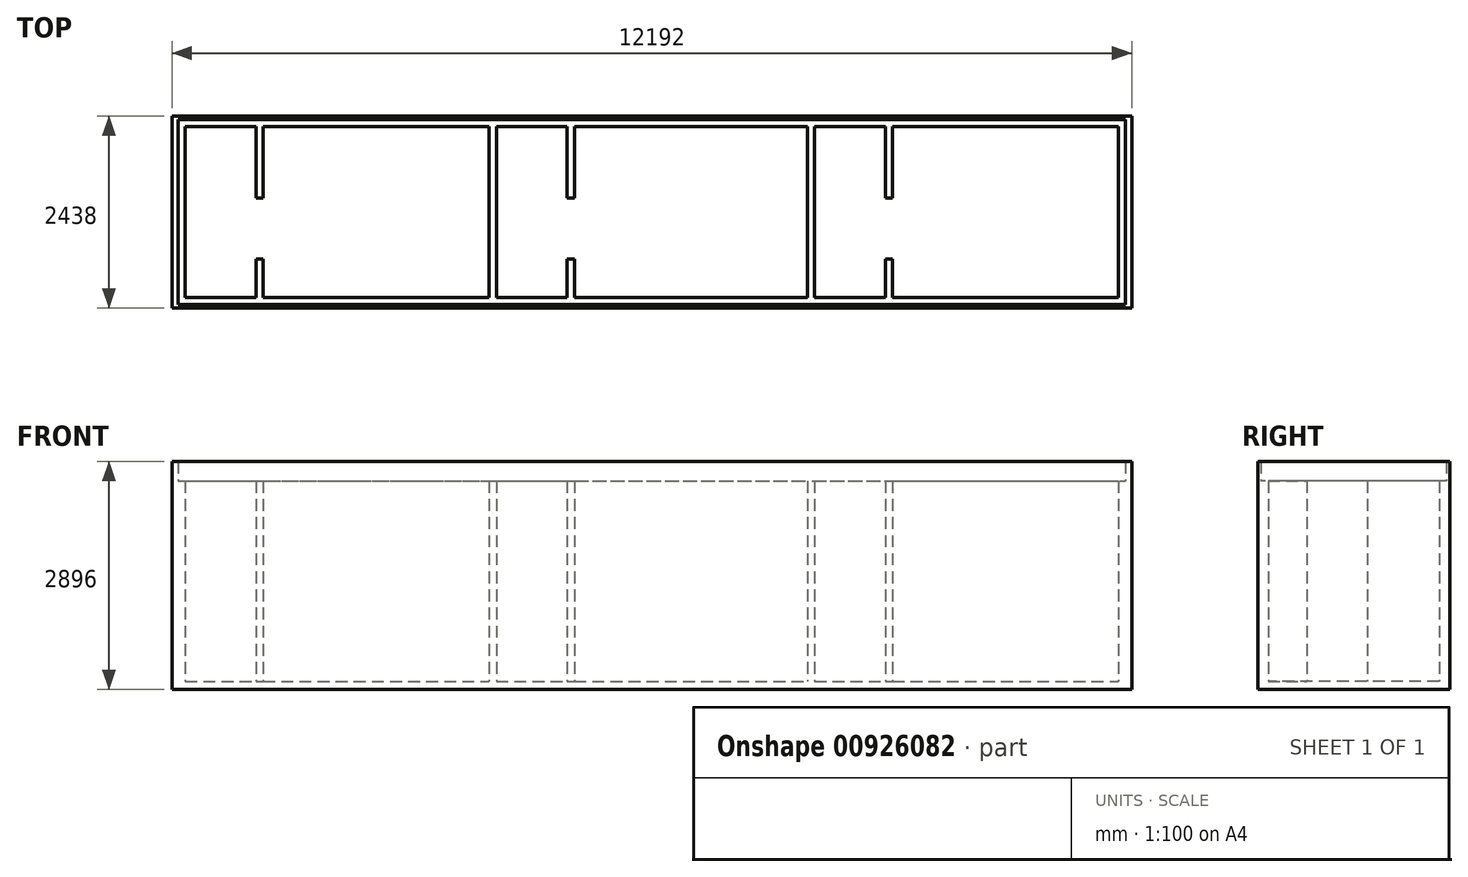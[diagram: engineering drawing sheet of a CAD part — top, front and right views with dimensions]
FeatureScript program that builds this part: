
annotation { "Feature Type Name" : "Feature", "Feature Type Description" : "" }
export const myFeature = defineFeature(function(context is Context, id is Id, definition is map)
    precondition{}
    {
        {
            var Q0;
            Q0=qCreatedBy(makeId("Top.planeOp"),FACE);
            var sketch = newSketch(context, id + "F0", { "sketchPlane" : qUnion([Q0])});
            skLineSegment(sketch, "E0.bottom", {"start": v(-6016, 1176) * mm, "end": v(6016, 1176) * mm});
            skLineSegment(sketch, "E0.top", {"start": v(-6016, -1176) * mm, "end": v(6016, -1176) * mm});
            skLineSegment(sketch, "E0.left", {"start": v(-6016, 1176) * mm, "end": v(-6016, -1176) * mm});
            skLineSegment(sketch, "E0.right", {"start": v(6016, 1176) * mm, "end": v(6016, -1176) * mm});
            skPoint(sketch, "E0.middle", {"position": v(0, 0) * mm});
            skLineSegment(sketch, "E1.bottom", {"start": v(-6096, 1219) * mm, "end": v(6096, 1219) * mm});
            skLineSegment(sketch, "E1.top", {"start": v(-6096, -1219) * mm, "end": v(6096, -1219) * mm});
            skLineSegment(sketch, "E1.left", {"start": v(-6096, 1219) * mm, "end": v(-6096, -1219) * mm});
            skLineSegment(sketch, "E1.right", {"start": v(6096, 1219) * mm, "end": v(6096, -1219) * mm});
            skSolve(sketch);
        }
        {
            var Q0;
            Q0=makeQuery(id+"F0.imprint","IMPRINT",FACE,{"disambiguationData":[TD([[makeQuery(id+"F0.imprint","IMPRINT",EDGE,{"derivedFrom":sQuery(id+"F0.wireOp",EDGE,"E0.bottom")}),1.0]])]});
            extrude(context, id + "F1", {"entities" : qUnion([Q0]), "depth" : 2896 * mm, "offsetDistance" : 25 * mm});
        }
        {
            var Q0;
            Q0=makeQuery(id+"F0.imprint","IMPRINT",FACE,{"disambiguationData":[TD([[makeQuery(id+"F0.imprint","IMPRINT",EDGE,{"derivedFrom":sQuery(id+"F0.wireOp",EDGE,"E0.bottom")}),-1.0]])]});
            extrude(context, id + "F2", {"entities" : qUnion([Q0]), "operationType" : NewBodyOperationType.ADD, "depth" : 99 * mm, "offsetDistance" : 25 * mm});
        }
        {
            var Q0;
            Q0=makeQuery(id+"F2.opExtrude","CAP_FACE",FACE,{"disambiguationData":[OSD([sQuery(id+"F0.wireOp",EDGE,"E0.bottom"),sQuery(id+"F0.wireOp",EDGE,"E0.top"),sQuery(id+"F0.wireOp",EDGE,"E0.left"),sQuery(id+"F0.wireOp",EDGE,"E0.right")])],"isStart":false});
            var sketch = newSketch(context, id + "F3", { "sketchPlane" : qUnion([Q0])});
            skLineSegment(sketch, "E2.bottom", {"start": v(-2065, 1176) * mm, "end": v(-1975, 1176) * mm});
            skLineSegment(sketch, "E2.top", {"start": v(-2065, -1176) * mm, "end": v(-1975, -1176) * mm});
            skLineSegment(sketch, "E2.left", {"start": v(-2065, 1176) * mm, "end": v(-2065, -1176) * mm});
            skLineSegment(sketch, "E2.right", {"start": v(-1975, 1176) * mm, "end": v(-1975, -1176) * mm});
            skLineSegment(sketch, "E3.bottom", {"start": v(1976, 1176) * mm, "end": v(2066, 1176) * mm});
            skLineSegment(sketch, "E3.top", {"start": v(1976, -1176) * mm, "end": v(2066, -1176) * mm});
            skLineSegment(sketch, "E3.left", {"start": v(1976, 1176) * mm, "end": v(1976, -1176) * mm});
            skLineSegment(sketch, "E3.right", {"start": v(2066, 1176) * mm, "end": v(2066, -1176) * mm});
            skLineSegment(sketch, "E4.bottom", {"start": v(-5026, 1176) * mm, "end": v(-4936, 1176) * mm});
            skLineSegment(sketch, "E4.top", {"start": v(-5026, 176) * mm, "end": v(-4936, 176) * mm});
            skLineSegment(sketch, "E4.left", {"start": v(-5026, 1176) * mm, "end": v(-5026, 176) * mm});
            skLineSegment(sketch, "E4.right", {"start": v(-4936, 1176) * mm, "end": v(-4936, 176) * mm});
            skLineSegment(sketch, "E5.bottom", {"start": v(-5026, -1176) * mm, "end": v(-4936, -1176) * mm});
            skLineSegment(sketch, "E5.top", {"start": v(-5026, -594) * mm, "end": v(-4936, -594) * mm});
            skLineSegment(sketch, "E5.left", {"start": v(-5026, -1176) * mm, "end": v(-5026, -594) * mm});
            skLineSegment(sketch, "E5.right", {"start": v(-4936, -1176) * mm, "end": v(-4936, -594) * mm});
            skLineSegment(sketch, "E6.bottom", {"start": v(-1075, 1176) * mm, "end": v(-985, 1176) * mm});
            skLineSegment(sketch, "E6.top", {"start": v(-1075, 176) * mm, "end": v(-985, 176) * mm});
            skLineSegment(sketch, "E6.left", {"start": v(-1075, 1176) * mm, "end": v(-1075, 176) * mm});
            skLineSegment(sketch, "E6.right", {"start": v(-985, 1176) * mm, "end": v(-985, 176) * mm});
            skLineSegment(sketch, "E7.bottom", {"start": v(-1075, -594) * mm, "end": v(-985, -594) * mm});
            skLineSegment(sketch, "E7.top", {"start": v(-1075, -1176) * mm, "end": v(-985, -1176) * mm});
            skLineSegment(sketch, "E7.left", {"start": v(-1075, -594) * mm, "end": v(-1075, -1176) * mm});
            skLineSegment(sketch, "E7.right", {"start": v(-985, -594) * mm, "end": v(-985, -1176) * mm});
            skLineSegment(sketch, "E8.bottom", {"start": v(2966, 1176) * mm, "end": v(3056, 1176) * mm});
            skLineSegment(sketch, "E8.top", {"start": v(2966, 176) * mm, "end": v(3056, 176) * mm});
            skLineSegment(sketch, "E8.left", {"start": v(2966, 1176) * mm, "end": v(2966, 176) * mm});
            skLineSegment(sketch, "E8.right", {"start": v(3056, 1176) * mm, "end": v(3056, 176) * mm});
            skLineSegment(sketch, "E9.bottom", {"start": v(2966, -1176) * mm, "end": v(3056, -1176) * mm});
            skLineSegment(sketch, "E9.top", {"start": v(2966, -594) * mm, "end": v(3056, -594) * mm});
            skLineSegment(sketch, "E9.left", {"start": v(2966, -1176) * mm, "end": v(2966, -594) * mm});
            skLineSegment(sketch, "E9.right", {"start": v(3056, -1176) * mm, "end": v(3056, -594) * mm});
            skLineSegment(sketch, "E10.bottom", {"start": v(-6016, 1176) * mm, "end": v(6016, 1176) * mm});
            skLineSegment(sketch, "E10.top", {"start": v(-6016, 1086) * mm, "end": v(6016, 1086) * mm});
            skLineSegment(sketch, "E10.left", {"start": v(-6016, 1176) * mm, "end": v(-6016, 1086) * mm});
            skLineSegment(sketch, "E10.right", {"start": v(6016, 1176) * mm, "end": v(6016, 1086) * mm});
            skLineSegment(sketch, "E11.bottom", {"start": v(6016, -1176) * mm, "end": v(-6016, -1176) * mm});
            skLineSegment(sketch, "E11.top", {"start": v(6016, -1086) * mm, "end": v(-6016, -1086) * mm});
            skLineSegment(sketch, "E11.left", {"start": v(6016, -1176) * mm, "end": v(6016, -1086) * mm});
            skLineSegment(sketch, "E11.right", {"start": v(-6016, -1176) * mm, "end": v(-6016, -1086) * mm});
            skLineSegment(sketch, "E12.bottom", {"start": v(-5926, -1086) * mm, "end": v(-6016, -1086) * mm});
            skLineSegment(sketch, "E12.top", {"start": v(-5926, 1086) * mm, "end": v(-6016, 1086) * mm});
            skLineSegment(sketch, "E12.left", {"start": v(-5926, -1086) * mm, "end": v(-5926, 1086) * mm});
            skLineSegment(sketch, "E12.right", {"start": v(-6016, -1086) * mm, "end": v(-6016, 1086) * mm});
            skLineSegment(sketch, "E13.bottom", {"start": v(6016, 1086) * mm, "end": v(5926, 1086) * mm});
            skLineSegment(sketch, "E13.top", {"start": v(6016, -1086) * mm, "end": v(5926, -1086) * mm});
            skLineSegment(sketch, "E13.left", {"start": v(6016, 1086) * mm, "end": v(6016, -1086) * mm});
            skLineSegment(sketch, "E13.right", {"start": v(5926, 1086) * mm, "end": v(5926, -1086) * mm});
            skSolve(sketch);
        }
        {
            var Q0;
            {var subQ2=sQuery(id+"F3.wireOp",EDGE,"E10.left");Q0=makeQuery(id+"F3.imprint","IMPRINT",FACE,{"disambiguationData":[TD([[makeQuery(id+"F3.imprint","IMPRINT",EDGE,{"derivedFrom":subQ2}),1.0]])]});}
            var Q1;
            {var subQ0=sQuery(id+"F3.wireOp",EDGE,"E4.bottom");Q1=makeQuery(id+"F3.imprint","IMPRINT",FACE,{"disambiguationData":[TD([[makeQuery(id+"F3.imprint","IMPRINT",EDGE,{"derivedFrom":subQ0}),-1.0]])]});}
            var Q2;
            {var subQ1=sQuery(id+"F3.wireOp",EDGE,"E2.left");var subQ3=sQuery(id+"F3.wireOp",EDGE,"E10.top");var subQ4=makeQuery(id+"F3.imprint","INTERSECT",VERTEX,{"derivedFrom":[subQ1,subQ3]});Q2=makeQuery(id+"F3.imprint","IMPRINT",FACE,{"disambiguationData":[TD([[makeQuery(id+"F3.imprint","IMPRINT",EDGE,{"disambiguationData":[TD([[subQ4,1.0]])],"derivedFrom":subQ3}),1.0]])]});}
            var Q3;
            {var subQ0=sQuery(id+"F3.wireOp",EDGE,"E4.top");Q3=makeQuery(id+"F3.imprint","IMPRINT",FACE,{"disambiguationData":[TD([[makeQuery(id+"F3.imprint","IMPRINT",EDGE,{"derivedFrom":subQ0}),1.0]])]});}
            var Q4;
            {var subQ0=sQuery(id+"F3.wireOp",EDGE,"E12.left");Q4=makeQuery(id+"F3.imprint","IMPRINT",FACE,{"disambiguationData":[TD([[makeQuery(id+"F3.imprint","IMPRINT",EDGE,{"derivedFrom":subQ0}),1.0]])]});}
            var Q5;
            {var subQ0=sQuery(id+"F3.wireOp",EDGE,"E11.right");Q5=makeQuery(id+"F3.imprint","IMPRINT",FACE,{"disambiguationData":[TD([[makeQuery(id+"F3.imprint","IMPRINT",EDGE,{"derivedFrom":subQ0}),1.0]])]});}
            var Q6;
            {var subQ0=sQuery(id+"F3.wireOp",EDGE,"E5.top");Q6=makeQuery(id+"F3.imprint","IMPRINT",FACE,{"disambiguationData":[TD([[makeQuery(id+"F3.imprint","IMPRINT",EDGE,{"derivedFrom":subQ0}),-1.0]])]});}
            var Q7;
            {var subQ0=sQuery(id+"F3.wireOp",EDGE,"E5.bottom");Q7=makeQuery(id+"F3.imprint","IMPRINT",FACE,{"disambiguationData":[TD([[makeQuery(id+"F3.imprint","IMPRINT",EDGE,{"derivedFrom":subQ0}),1.0]])]});}
            var Q8;
            {var subQ3=sQuery(id+"F3.wireOp",EDGE,"E11.top");var subQ5=sQuery(id+"F3.wireOp",EDGE,"E5.right");var subQ7=makeQuery(id+"F3.imprint","INTERSECT",VERTEX,{"derivedFrom":[subQ5,subQ3]});Q8=makeQuery(id+"F3.imprint","IMPRINT",FACE,{"disambiguationData":[TD([[makeQuery(id+"F3.imprint","IMPRINT",EDGE,{"disambiguationData":[TD([[subQ7,1.0]])],"derivedFrom":subQ3}),1.0]])]});}
            var Q9;
            {var subQ0=sQuery(id+"F3.wireOp",EDGE,"E10.top");var subQ1=sQuery(id+"F3.wireOp",EDGE,"E2.left");var subQ2=makeQuery(id+"F3.imprint","INTERSECT",VERTEX,{"derivedFrom":[subQ1,subQ0]});Q9=makeQuery(id+"F3.imprint","IMPRINT",FACE,{"disambiguationData":[TD([[makeQuery(id+"F3.imprint","IMPRINT",EDGE,{"disambiguationData":[TD([[subQ2,-1.0]])],"derivedFrom":subQ1}),1.0]])]});}
            var Q10;
            {var subQ0=sQuery(id+"F3.wireOp",EDGE,"E2.bottom");Q10=makeQuery(id+"F3.imprint","IMPRINT",FACE,{"disambiguationData":[TD([[makeQuery(id+"F3.imprint","IMPRINT",EDGE,{"derivedFrom":subQ0}),-1.0]])]});}
            var Q11;
            {var subQ1=sQuery(id+"F3.wireOp",EDGE,"E2.right");var subQ3=sQuery(id+"F3.wireOp",EDGE,"E10.top");var subQ4=makeQuery(id+"F3.imprint","INTERSECT",VERTEX,{"derivedFrom":[subQ1,subQ3]});Q11=makeQuery(id+"F3.imprint","IMPRINT",FACE,{"disambiguationData":[TD([[makeQuery(id+"F3.imprint","IMPRINT",EDGE,{"disambiguationData":[TD([[subQ4,-1.0]])],"derivedFrom":subQ3}),1.0]])]});}
            var Q12;
            {var subQ0=sQuery(id+"F3.wireOp",EDGE,"E6.bottom");Q12=makeQuery(id+"F3.imprint","IMPRINT",FACE,{"disambiguationData":[TD([[makeQuery(id+"F3.imprint","IMPRINT",EDGE,{"derivedFrom":subQ0}),-1.0]])]});}
            var Q13;
            {var subQ1=sQuery(id+"F3.wireOp",EDGE,"E3.left");var subQ3=sQuery(id+"F3.wireOp",EDGE,"E10.top");var subQ4=makeQuery(id+"F3.imprint","INTERSECT",VERTEX,{"derivedFrom":[subQ1,subQ3]});Q13=makeQuery(id+"F3.imprint","IMPRINT",FACE,{"disambiguationData":[TD([[makeQuery(id+"F3.imprint","IMPRINT",EDGE,{"disambiguationData":[TD([[subQ4,1.0]])],"derivedFrom":subQ3}),1.0]])]});}
            var Q14;
            {var subQ0=sQuery(id+"F3.wireOp",EDGE,"E6.top");Q14=makeQuery(id+"F3.imprint","IMPRINT",FACE,{"disambiguationData":[TD([[makeQuery(id+"F3.imprint","IMPRINT",EDGE,{"derivedFrom":subQ0}),1.0]])]});}
            var Q15;
            {var subQ1=sQuery(id+"F3.wireOp",EDGE,"E2.right");var subQ3=sQuery(id+"F3.wireOp",EDGE,"E11.top");var subQ4=makeQuery(id+"F3.imprint","INTERSECT",VERTEX,{"derivedFrom":[subQ1,subQ3]});Q15=makeQuery(id+"F3.imprint","IMPRINT",FACE,{"disambiguationData":[TD([[makeQuery(id+"F3.imprint","IMPRINT",EDGE,{"disambiguationData":[TD([[subQ4,1.0]])],"derivedFrom":subQ3}),1.0]])]});}
            var Q16;
            {var subQ0=sQuery(id+"F3.wireOp",EDGE,"E2.top");Q16=makeQuery(id+"F3.imprint","IMPRINT",FACE,{"disambiguationData":[TD([[makeQuery(id+"F3.imprint","IMPRINT",EDGE,{"derivedFrom":subQ0}),1.0]])]});}
            var Q17;
            {var subQ0=sQuery(id+"F3.wireOp",EDGE,"E7.bottom");Q17=makeQuery(id+"F3.imprint","IMPRINT",FACE,{"disambiguationData":[TD([[makeQuery(id+"F3.imprint","IMPRINT",EDGE,{"derivedFrom":subQ0}),-1.0]])]});}
            var Q18;
            {var subQ0=sQuery(id+"F3.wireOp",EDGE,"E7.top");Q18=makeQuery(id+"F3.imprint","IMPRINT",FACE,{"disambiguationData":[TD([[makeQuery(id+"F3.imprint","IMPRINT",EDGE,{"derivedFrom":subQ0}),1.0]])]});}
            var Q19;
            {var subQ1=sQuery(id+"F3.wireOp",EDGE,"E3.left");var subQ3=sQuery(id+"F3.wireOp",EDGE,"E11.top");var subQ4=makeQuery(id+"F3.imprint","INTERSECT",VERTEX,{"derivedFrom":[subQ1,subQ3]});Q19=makeQuery(id+"F3.imprint","IMPRINT",FACE,{"disambiguationData":[TD([[makeQuery(id+"F3.imprint","IMPRINT",EDGE,{"disambiguationData":[TD([[subQ4,-1.0]])],"derivedFrom":subQ3}),1.0]])]});}
            var Q20;
            {var subQ0=sQuery(id+"F3.wireOp",EDGE,"E10.top");var subQ1=sQuery(id+"F3.wireOp",EDGE,"E3.left");var subQ2=makeQuery(id+"F3.imprint","INTERSECT",VERTEX,{"derivedFrom":[subQ1,subQ0]});Q20=makeQuery(id+"F3.imprint","IMPRINT",FACE,{"disambiguationData":[TD([[makeQuery(id+"F3.imprint","IMPRINT",EDGE,{"disambiguationData":[TD([[subQ2,-1.0]])],"derivedFrom":subQ1}),1.0]])]});}
            var Q21;
            {var subQ0=sQuery(id+"F3.wireOp",EDGE,"E3.bottom");Q21=makeQuery(id+"F3.imprint","IMPRINT",FACE,{"disambiguationData":[TD([[makeQuery(id+"F3.imprint","IMPRINT",EDGE,{"derivedFrom":subQ0}),-1.0]])]});}
            var Q22;
            {var subQ0=sQuery(id+"F3.wireOp",EDGE,"E3.top");Q22=makeQuery(id+"F3.imprint","IMPRINT",FACE,{"disambiguationData":[TD([[makeQuery(id+"F3.imprint","IMPRINT",EDGE,{"derivedFrom":subQ0}),1.0]])]});}
            var Q23;
            {var subQ3=sQuery(id+"F3.wireOp",EDGE,"E11.top");var subQ5=sQuery(id+"F3.wireOp",EDGE,"E9.left");var subQ7=makeQuery(id+"F3.imprint","INTERSECT",VERTEX,{"derivedFrom":[subQ5,subQ3]});Q23=makeQuery(id+"F3.imprint","IMPRINT",FACE,{"disambiguationData":[TD([[makeQuery(id+"F3.imprint","IMPRINT",EDGE,{"disambiguationData":[TD([[subQ7,-1.0]])],"derivedFrom":subQ3}),1.0]])]});}
            var Q24;
            {var subQ0=sQuery(id+"F3.wireOp",EDGE,"E9.bottom");Q24=makeQuery(id+"F3.imprint","IMPRINT",FACE,{"disambiguationData":[TD([[makeQuery(id+"F3.imprint","IMPRINT",EDGE,{"derivedFrom":subQ0}),1.0]])]});}
            var Q25;
            {var subQ0=sQuery(id+"F3.wireOp",EDGE,"E11.left");Q25=makeQuery(id+"F3.imprint","IMPRINT",FACE,{"disambiguationData":[TD([[makeQuery(id+"F3.imprint","IMPRINT",EDGE,{"derivedFrom":subQ0}),-1.0]])]});}
            var Q26;
            {var subQ0=sQuery(id+"F3.wireOp",EDGE,"E9.top");Q26=makeQuery(id+"F3.imprint","IMPRINT",FACE,{"disambiguationData":[TD([[makeQuery(id+"F3.imprint","IMPRINT",EDGE,{"derivedFrom":subQ0}),-1.0]])]});}
            var Q27;
            {var subQ0=sQuery(id+"F3.wireOp",EDGE,"E8.top");Q27=makeQuery(id+"F3.imprint","IMPRINT",FACE,{"disambiguationData":[TD([[makeQuery(id+"F3.imprint","IMPRINT",EDGE,{"derivedFrom":subQ0}),1.0]])]});}
            var Q28;
            {var subQ0=sQuery(id+"F3.wireOp",EDGE,"E8.bottom");Q28=makeQuery(id+"F3.imprint","IMPRINT",FACE,{"disambiguationData":[TD([[makeQuery(id+"F3.imprint","IMPRINT",EDGE,{"derivedFrom":subQ0}),-1.0]])]});}
            var Q29;
            {var subQ1=sQuery(id+"F3.wireOp",EDGE,"E3.right");var subQ3=sQuery(id+"F3.wireOp",EDGE,"E10.top");var subQ4=makeQuery(id+"F3.imprint","INTERSECT",VERTEX,{"derivedFrom":[subQ1,subQ3]});Q29=makeQuery(id+"F3.imprint","IMPRINT",FACE,{"disambiguationData":[TD([[makeQuery(id+"F3.imprint","IMPRINT",EDGE,{"disambiguationData":[TD([[subQ4,-1.0]])],"derivedFrom":subQ3}),1.0]])]});}
            var Q30;
            {var subQ0=sQuery(id+"F3.wireOp",EDGE,"E10.right");Q30=makeQuery(id+"F3.imprint","IMPRINT",FACE,{"disambiguationData":[TD([[makeQuery(id+"F3.imprint","IMPRINT",EDGE,{"derivedFrom":subQ0}),-1.0]])]});}
            var Q31;
            {var subQ0=sQuery(id+"F3.wireOp",EDGE,"E13.left");Q31=makeQuery(id+"F3.imprint","IMPRINT",FACE,{"disambiguationData":[TD([[makeQuery(id+"F3.imprint","IMPRINT",EDGE,{"derivedFrom":subQ0}),-1.0]])]});}
            extrude(context, id + "F4", {"entities" : qUnion([Q0, Q1, Q2, Q3, Q4, Q5, Q6, Q7, Q8, Q9, Q10, Q11, Q12, Q13, Q14, Q15, Q16, Q17, Q18, Q19, Q20, Q21, Q22, Q23, Q24, Q25, Q26, Q27, Q28, Q29, Q30, Q31]), "operationType" : NewBodyOperationType.ADD, "depth" : 2550 * mm, "offsetDistance" : 25 * mm});
        }
    });
